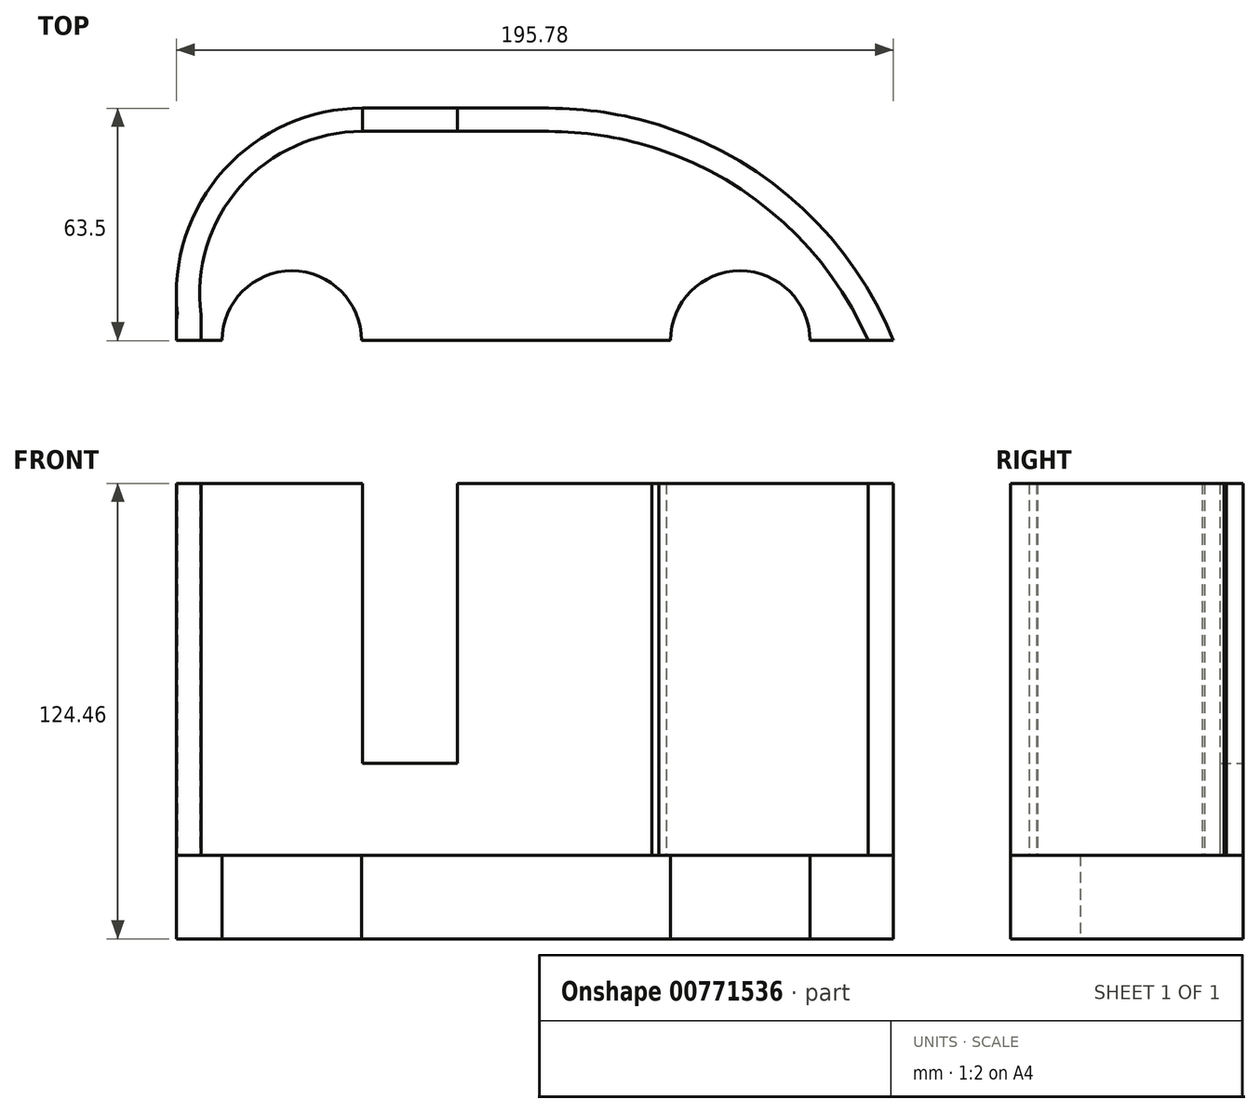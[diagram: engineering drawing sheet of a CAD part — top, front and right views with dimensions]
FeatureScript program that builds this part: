
annotation { "Feature Type Name" : "Feature", "Feature Type Description" : "" }
export const myFeature = defineFeature(function(context is Context, id is Id, definition is map)
    precondition{}
    {
        {
            var Q0;
            Q0=qCreatedBy(makeId("Top.planeOp"),FACE);
            var sketch = newSketch(context, id + "F0", { "sketchPlane" : qUnion([Q0])});
            skLineSegment(sketch, "E0.bottom", {"start": v(3.35, 51.42) * mm, "end": v(54.15, 51.42) * mm});
            skLineSegment(sketch, "E0.top", {"start": v(-47.45, -12.08) * mm, "end": v(-34.96, -12.08) * mm});
            skLineSegment(sketch, "E0.left", {"start": v(-47.45, 0.62) * mm, "end": v(-47.45, -12.08) * mm});
            skPoint(sketch, "E1.visualSharp", {"position": v(155.75, 51.42) * mm});
            skArc(sketch, "E1.filletArc", {"start": v(148.33, -12.08) * mm, "mid": v(110.95, 34.07) * mm, "end": v(54.15, 51.42) * mm});
            skPoint(sketch, "E2.visualSharp", {"position": v(-47.45, 51.42) * mm});
            skArc(sketch, "E2.filletArc", {"start": v(3.35, 51.42) * mm, "mid": v(-32.57, 36.55) * mm, "end": v(-47.45, 0.62) * mm});
            skArc(sketch, "E3", {"start": v(3.14, -12.08) * mm, "mid": v(-15.9, 6.97) * mm, "end": v(-34.96, -12.08) * mm});
            skArc(sketch, "E4", {"start": v(125.54, -12.08) * mm, "mid": v(106.49, 6.97) * mm, "end": v(87.44, -12.08) * mm});
            skLineSegment(sketch, "E5.trimOffspring", {"start": v(3.14, -12.08) * mm, "end": v(87.44, -12.08) * mm});
            skLineSegment(sketch, "E6.trimOffspring", {"start": v(125.54, -12.08) * mm, "end": v(148.33, -12.08) * mm});
            skSolve(sketch);
        }
        {
            var Q0;
            Q0 = qSketchRegion(id + "F0", true);
            extrude(context, id + "F1", {"entities" : qUnion([Q0]), "depth" : 22.86 * mm, "offsetDistance" : 25.4 * mm});
        }
        {
            var Q0;
            Q0=makeQuery(id+"F1.opExtrude","CAP_FACE",FACE,{"disambiguationData":[OSD([sQuery(id+"F0.wireOp",EDGE,"E0.bottom"),sQuery(id+"F0.wireOp",EDGE,"E0.top"),sQuery(id+"F0.wireOp",EDGE,"E0.left"),sQuery(id+"F0.wireOp",EDGE,"E1.filletArc"),sQuery(id+"F0.wireOp",EDGE,"E2.filletArc"),sQuery(id+"F0.wireOp",EDGE,"E3"),sQuery(id+"F0.wireOp",EDGE,"E4"),sQuery(id+"F0.wireOp",EDGE,"E5.trimOffspring"),sQuery(id+"F0.wireOp",EDGE,"E6.trimOffspring")])],"isStart":false});
            var sketch = newSketch(context, id + "F2", { "sketchPlane" : qUnion([Q0])});
            skArc(sketch, "E7", {"start": v(3.35, 51.42) * mm, "mid": v(-34.44, 34.57) * mm, "end": v(-47.16, -4.8) * mm});
            skPoint(sketch, "E7.first.point", {"position": v(-47.45, 0.62) * mm});
            skPoint(sketch, "E7.second.point", {"position": v(3.35, 51.42) * mm});
            skPoint(sketch, "E7.third.point", {"position": v(-29.86, 39.07) * mm});
            skArc(sketch, "E8", {"start": v(148.33, -12.08) * mm, "mid": v(123.72, 23.87) * mm, "end": v(86.3, 46.2) * mm});
            skPoint(sketch, "E8.first.point", {"position": v(148.33, -12.08) * mm});
            skPoint(sketch, "E8.second.point", {"position": v(54.15, 51.42) * mm});
            skPoint(sketch, "E8.third.point", {"position": v(86.3, 46.2) * mm});
            skPoint(sketch, "E9.first.point", {"position": v(-47.45, -12.08) * mm});
            skPoint(sketch, "E9.second.point", {"position": v(9.05, -6.18) * mm});
            skPoint(sketch, "E9.third.point", {"position": v(4.58, 6.04) * mm});
            skArc(sketch, "E10", {"start": v(36.97, 51.42) * mm, "mid": v(26.45, 51.58) * mm, "end": v(15.93, 51.42) * mm});
            skPoint(sketch, "E10.first.point", {"position": v(36.97, 51.42) * mm});
            skPoint(sketch, "E10.second.point", {"position": v(15.93, 51.42) * mm});
            skPoint(sketch, "E10.third.point", {"position": v(84.24, 46.87) * mm});
            skArc(sketch, "E11.trimOffspring", {"start": v(-47.16, -4.8) * mm, "mid": v(-47.54, -8.43) * mm, "end": v(-47.45, -12.08) * mm});
            skArc(sketch, "E12.trimOffspring", {"start": v(84.24, 46.87) * mm, "mid": v(69.37, 50.28) * mm, "end": v(54.15, 51.42) * mm});
            skLineSegment(sketch, "E13", {"start": v(84.24, 46.87) * mm, "end": v(86.3, 46.2) * mm});
            skLineSegment(sketch, "E14", {"start": v(3.35, 51.42) * mm, "end": v(15.93, 51.42) * mm});
            skArc(sketch, "E15.1", {"start": v(3.35, 45.07) * mm, "mid": v(-30.02, 30) * mm, "end": v(-40.74, -5.02) * mm});
            skLineSegment(sketch, "E16", {"start": v(36.97, 51.42) * mm, "end": v(54.15, 51.42) * mm});
            skLineSegment(sketch, "E17.0", {"start": v(3.35, 45.07) * mm, "end": v(54.15, 45.07) * mm});
            skArc(sketch, "E18.0", {"start": v(82.33, 40.81) * mm, "mid": v(68.4, 44) * mm, "end": v(54.15, 45.07) * mm});
            skLineSegment(sketch, "E18.1", {"start": v(82.33, 40.81) * mm, "end": v(84.33, 40.17) * mm});
            skArc(sketch, "E18.2", {"start": v(141.45, -12.08) * mm, "mid": v(118.43, 20.1) * mm, "end": v(84.33, 40.17) * mm});
            skLineSegment(sketch, "E19", {"start": v(148.33, -12.08) * mm, "end": v(141.45, -12.08) * mm});
            skPoint(sketch, "E20.orphan", {"position": v(136.94, -12.08) * mm});
            skLineSegment(sketch, "E21", {"start": v(-47.45, -12.08) * mm, "end": v(-40.74, -12.08) * mm});
            skLineSegment(sketch, "E22", {"start": v(-40.74, -5.02) * mm, "end": v(-40.74, -12.08) * mm});
            skSolve(sketch);
        }
        {
            var Q0;
            Q0=makeQuery(id+"F2.imprint","IMPRINT",FACE,{"disambiguationData":[TD([[makeQuery(id+"F2.imprint","IMPRINT",EDGE,{"derivedFrom":sQuery(id+"F2.wireOp",EDGE,"E8")}),1.0]])]});
            extrude(context, id + "F3", {"entities" : qUnion([Q0]), "depth" : 101.6 * mm, "offsetDistance" : 25.4 * mm});
        }
        {
            var Q0;
            Q0=makeQuery(id+"F3.opExtrude","SWEPT_FACE",FACE,{"disambiguationData":[OSD([sQuery(id+"F0.wireOp",EDGE,"E0.bottom"),sQuery(id+"F2.wireOp",EDGE,"E14"),sQuery(id+"F2.wireOp",EDGE,"E16")])]});
            var sketch = newSketch(context, id + "F4", { "sketchPlane" : qUnion([Q0])});
            skLineSegment(sketch, "E23.bottom", {"start": v(-3.35, 124.46) * mm, "end": v(-29.31, 124.46) * mm});
            skLineSegment(sketch, "E23.top", {"start": v(-3.35, 47.96) * mm, "end": v(-29.31, 47.96) * mm});
            skLineSegment(sketch, "E23.left", {"start": v(-3.35, 124.46) * mm, "end": v(-3.35, 47.96) * mm});
            skLineSegment(sketch, "E23.right", {"start": v(-29.31, 124.46) * mm, "end": v(-29.31, 47.96) * mm});
            skSolve(sketch);
        }
        {
            var Q0;
            Q0 = qSketchRegion(id + "F4", true);
            extrude(context, id + "F5", {"entities" : qUnion([Q0]), "operationType" : NewBodyOperationType.REMOVE, "oppositeDirection" : true, "depth" : 25.4 * mm, "offsetDistance" : 25.4 * mm});
        }
    });
